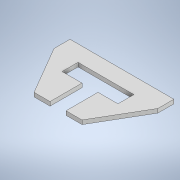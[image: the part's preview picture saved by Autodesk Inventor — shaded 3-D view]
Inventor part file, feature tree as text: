
AUTODESK INVENTOR PART (.ipt)
format: ipt  version: 2022.2 (Build 262287030, 287C)  size: 114,688 bytes
history: native  units: in
note: dims shown in document units (in); Inventor stores cm internally (conversion verified against a paired STEP export)
features: extrude x1, sketch x1
ambient origin geometry x8: Origin, YZ Plane, XZ Plane, XY Plane, X Axis, Y Axis, Z Axis, Center Point
bodies: Solid1 (feature_tree)
feature tree (2):
  extrude  "Extrusion1"  Depth=1.5in
  sketch  "Sketch1"  dims[d0=6.5in d3=1.5in d4=1.0in d5=1.0in d6=4.0in d7=1.75in d8=2.75in d9=4.75in d10=1.0in d11=3.5in d12=1.0in d13=0.25in d14=0.0in]
